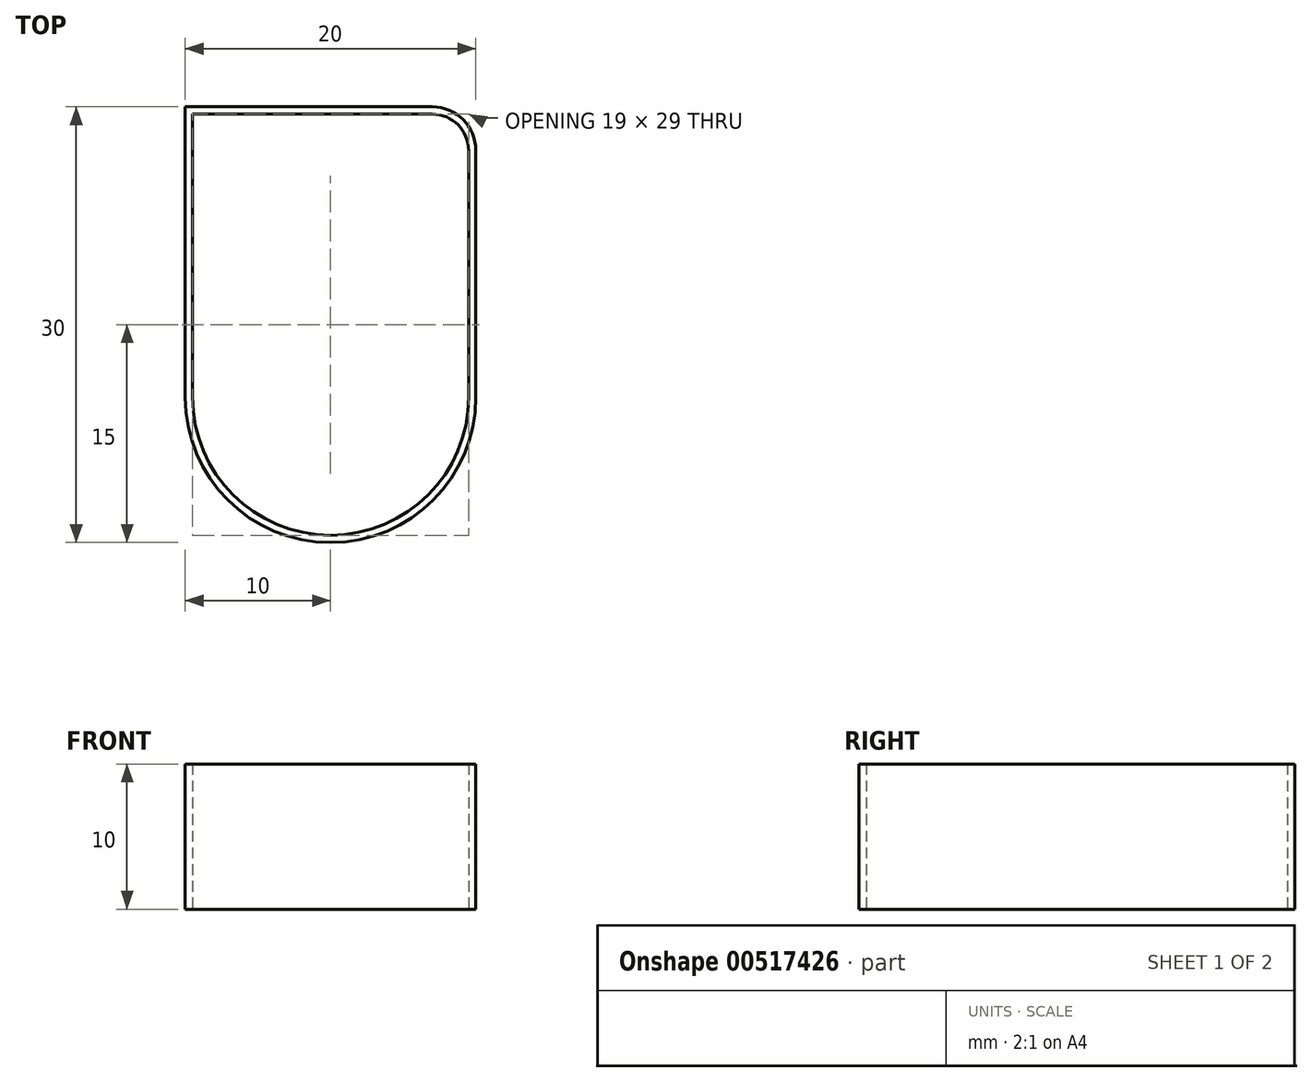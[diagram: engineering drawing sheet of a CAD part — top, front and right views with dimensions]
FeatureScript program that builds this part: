
annotation { "Feature Type Name" : "Feature", "Feature Type Description" : "" }
export const myFeature = defineFeature(function(context is Context, id is Id, definition is map)
    precondition{}
    {
        {
            var Q0;
            Q0=qCreatedBy(makeId("Top.planeOp"),FACE);
            var sketch = newSketch(context, id + "F0", { "sketchPlane" : qUnion([Q0])});
            skLineSegment(sketch, "E0", {"start": v(-10, 10) * mm, "end": v(-10, -10) * mm});
            skLineSegment(sketch, "E1", {"start": v(-10, 10) * mm, "end": v(7, 10) * mm});
            skArc(sketch, "E2", {"start": v(10, 7) * mm, "mid": v(9.12, 9.12) * mm, "end": v(7, 10) * mm});
            skLineSegment(sketch, "E3", {"start": v(10, 7) * mm, "end": v(10, -10) * mm});
            skArc(sketch, "E4", {"start": v(-10, -10) * mm, "mid": v(0, -20) * mm, "end": v(10, -10) * mm});
            skArc(sketch, "E5.0", {"start": v(9.5, 7) * mm, "mid": v(8.77, 8.77) * mm, "end": v(7, 9.5) * mm});
            skLineSegment(sketch, "E5.1", {"start": v(-9.5, 9.5) * mm, "end": v(7, 9.5) * mm});
            skLineSegment(sketch, "E5.2", {"start": v(9.5, 7) * mm, "end": v(9.5, -10) * mm});
            skArc(sketch, "E5.3", {"start": v(-9.5, -10) * mm, "mid": v(0, -19.5) * mm, "end": v(9.5, -10) * mm});
            skLineSegment(sketch, "E5.4", {"start": v(-9.5, 9.5) * mm, "end": v(-9.5, -10) * mm});
            skPoint(sketch, "E6", {"position": v(-10, 0) * mm});
            skSolve(sketch);
        }
        {
            var Q0;
            Q0=makeQuery(id+"F0.imprint","IMPRINT",FACE,{"disambiguationData":[TD([[makeQuery(id+"F0.imprint","IMPRINT",EDGE,{"derivedFrom":sQuery(id+"F0.wireOp",EDGE,"E0")}),1.0]])]});
            extrude(context, id + "F1", {"entities" : qUnion([Q0]), "depth" : 10 * mm, "offsetDistance" : 25 * mm});
        }
    });
